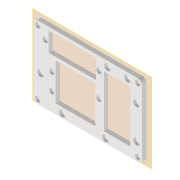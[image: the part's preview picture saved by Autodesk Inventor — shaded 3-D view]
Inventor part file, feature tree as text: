
AUTODESK INVENTOR PART (.ipt)
format: ipt  version: 2022.5 (Build 265521000, 521)  size: 232,448 bytes
history: native  units: mm
features: other x3, plane x2, extrude x2, projected_geometry x2, hole x1, reference x1, sketch x1
ambient origin geometry x8: Origin, YZ Plane, XZ Plane, XY Plane, X Axis, Y Axis, Z Axis, Center Point
bodies: Volumenkörper1 (feature_tree)
feature tree (12):
  plane  "Arbeitsebene1"
  extrude  "Extrusion1"  Depth=3.2mm
  hole  "Bohrung1"  [1 undecoded]
  plane  "Arbeitsebene2"
  extrude  "Extrusion6"  Depth=3.2mm
  reference  "Referenz1"
  projected_geometry  "Projizierte Kontur1"
  sketch  "Skizze7"  dims[d0=2.8mm d1=2.8mm d2=2.8mm d3=2.8mm d4=5.0mm d5=0.0mm d15=2.9mm d16=6.0mm d17=6.5mm d18=3.0mm d19=90.0deg d20=8.0mm d21=20.594885mm d29=4.0mm d33=8.0mm d34=8.0mm d35=8.0mm d36=8.0mm d37=8.0mm d38=8.0mm d39=8.0mm d40=3.2mm d41=0.0mm]
  projected_geometry  "Projizierte Kontur2"
  other  "Assembly_Guinardia_V3.iam"
  other  "10_Wellplate_base_v2:1"
  other  "Assembly_Guinardia_V2.iam"
note: 1 required parameter value undecoded (feature->parameter linkage not recoverable at this tier; creation-order binding heuristic only, values carry confidence <= 0.55)
